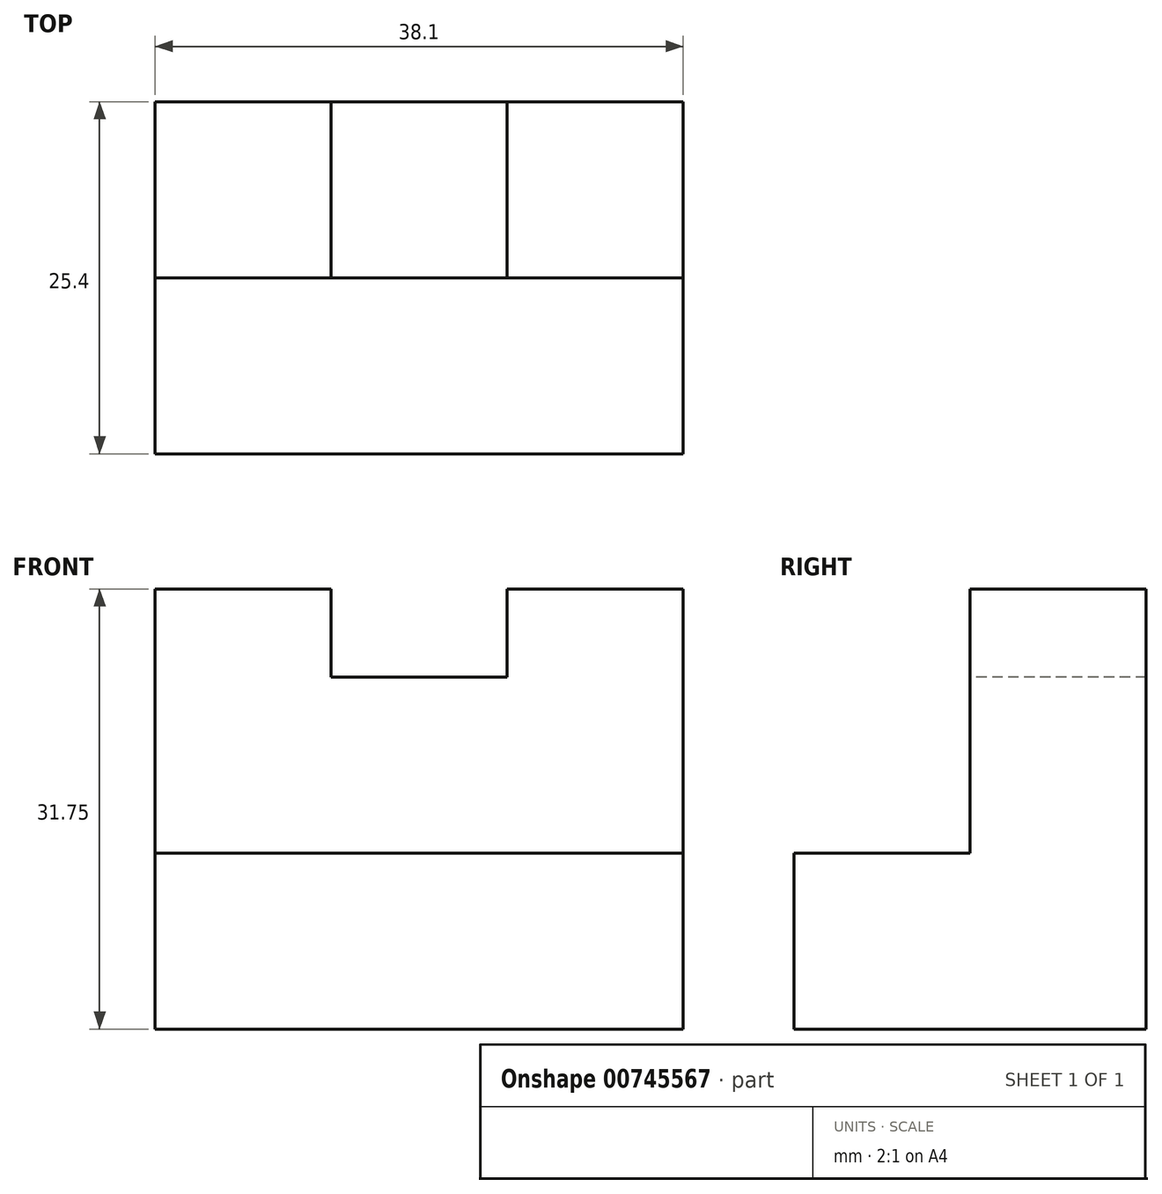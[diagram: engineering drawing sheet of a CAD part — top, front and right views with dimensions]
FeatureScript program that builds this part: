
annotation { "Feature Type Name" : "Feature", "Feature Type Description" : "" }
export const myFeature = defineFeature(function(context is Context, id is Id, definition is map)
    precondition{}
    {
        {
            var Q0;
            Q0=qCreatedBy(makeId("Right.planeOp"),FACE);
            var sketch = newSketch(context, id + "F0", { "sketchPlane" : qUnion([Q0])});
            skLineSegment(sketch, "E0", {"start": v(0, 0) * mm, "end": v(-25.4, 0) * mm});
            skLineSegment(sketch, "E1", {"start": v(-25.4, 0) * mm, "end": v(-25.4, 12.7) * mm});
            skLineSegment(sketch, "E2", {"start": v(-25.4, 12.7) * mm, "end": v(-12.7, 12.7) * mm});
            skLineSegment(sketch, "E3", {"start": v(-12.7, 12.7) * mm, "end": v(-12.7, 31.75) * mm});
            skLineSegment(sketch, "E4", {"start": v(-12.7, 31.75) * mm, "end": v(0, 31.75) * mm});
            skLineSegment(sketch, "E5", {"start": v(0, 31.75) * mm, "end": v(0, 0) * mm});
            skSolve(sketch);
        }
        {
            var Q0;
            Q0=qSketchRegion(id+"F0",true);
            extrude(context, id + "F1", {"entities" : qUnion([Q0]), "depth" : 38.1 * mm, "offsetDistance" : 25.4 * mm});
        }
        {
            var Q0;
            Q0=makeQuery(id+"F1.opExtrude","SWEPT_FACE",FACE,{"disambiguationData":[OSD([sQuery(id+"F0.wireOp",EDGE,"E4")])]});
            var sketch = newSketch(context, id + "F2", { "sketchPlane" : qUnion([Q0])});
            skLineSegment(sketch, "E6", {"start": v(0, 0) * mm, "end": v(12.7, 0) * mm});
            skLineSegment(sketch, "E7", {"start": v(12.7, 0) * mm, "end": v(12.7, -12.7) * mm});
            skLineSegment(sketch, "E8", {"start": v(12.7, -12.7) * mm, "end": v(25.4, -12.7) * mm});
            skLineSegment(sketch, "E9", {"start": v(25.4, -12.7) * mm, "end": v(25.4, 0) * mm});
            skSolve(sketch);
        }
        {
            var Q0;
            Q0=qSketchRegion(id+"F2",true);
            var Q1;
            {var subQ0=sQuery(id+"F2.wireOp",EDGE,"E7");Q1=makeQuery(id+"F2.imprint","IMPRINT",FACE,{"disambiguationData":[TD([[makeQuery(id+"F2.imprint","IMPRINT",EDGE,{"derivedFrom":subQ0}),1.0]])]});}
            extrude(context, id + "F3", {"entities" : qUnion([Q0, Q1]), "operationType" : NewBodyOperationType.REMOVE, "oppositeDirection" : true, "depth" : 6.35 * mm, "offsetDistance" : 25.4 * mm});
        }
    });
